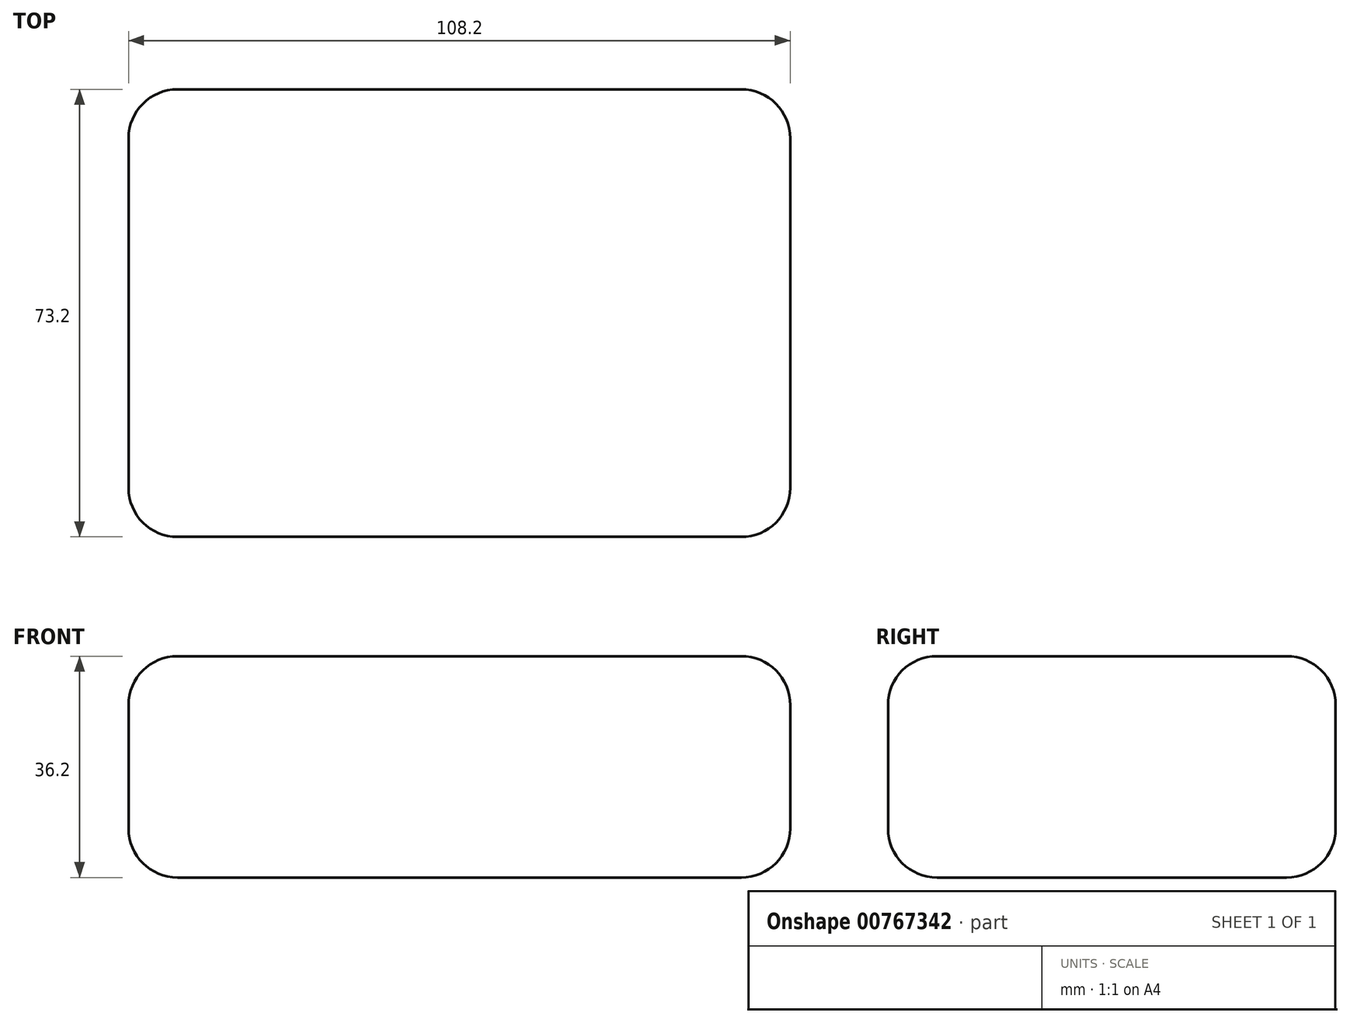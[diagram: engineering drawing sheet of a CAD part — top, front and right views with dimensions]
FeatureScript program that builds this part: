
annotation { "Feature Type Name" : "Feature", "Feature Type Description" : "" }
export const myFeature = defineFeature(function(context is Context, id is Id, definition is map)
    precondition{}
    {
        {
            var Q0;
            Q0=qCreatedBy(makeId("Top.planeOp"),FACE);
            var sketch = newSketch(context, id + "F0", { "sketchPlane" : qUnion([Q0])});
            skLineSegment(sketch, "E0.bottom", {"start": v(54.1, -36.6) * mm, "end": v(-54.1, -36.6) * mm});
            skLineSegment(sketch, "E0.top", {"start": v(54.1, 36.6) * mm, "end": v(-54.1, 36.6) * mm});
            skLineSegment(sketch, "E0.left", {"start": v(54.1, -36.6) * mm, "end": v(54.1, 36.6) * mm});
            skLineSegment(sketch, "E0.right", {"start": v(-54.1, -36.6) * mm, "end": v(-54.1, 36.6) * mm});
            skPoint(sketch, "E0.middle", {"position": v(0, 0) * mm});
            skSolve(sketch);
        }
        {
            var Q0;
            Q0 = qSketchRegion(id + "F0", true);
            extrude(context, id + "F1", {"entities" : qUnion([Q0]), "depth" : 36.2 * mm, "offsetDistance" : 25 * mm});
        }
        {
            var Q0;
            Q0=makeQuery(id+"F1.opExtrude","CAP_FACE",FACE,{"disambiguationData":[OSD([sQuery(id+"F0.wireOp",EDGE,"E0.bottom"),sQuery(id+"F0.wireOp",EDGE,"E0.top"),sQuery(id+"F0.wireOp",EDGE,"E0.left"),sQuery(id+"F0.wireOp",EDGE,"E0.right")])],"isStart":false});
            var Q1;
            Q1=makeQuery(id+"F1.opExtrude","CAP_EDGE",EDGE,{"disambiguationData":[OSD([sQuery(id+"F0.wireOp",EDGE,"E0.bottom")])],"isStart":true});
            var Q2;
            Q2=makeQuery(id+"F1.opExtrude","CAP_EDGE",EDGE,{"disambiguationData":[OSD([sQuery(id+"F0.wireOp",EDGE,"E0.left")])],"isStart":true});
            var Q3;
            Q3=makeQuery(id+"F1.opExtrude","CAP_FACE",FACE,{"disambiguationData":[OSD([sQuery(id+"F0.wireOp",EDGE,"E0.bottom"),sQuery(id+"F0.wireOp",EDGE,"E0.top"),sQuery(id+"F0.wireOp",EDGE,"E0.left"),sQuery(id+"F0.wireOp",EDGE,"E0.right")])],"isStart":true});
            var Q4;
            Q4=makeQuery(id+"F1.opExtrude","SWEPT_FACE",FACE,{"disambiguationData":[OSD([sQuery(id+"F0.wireOp",EDGE,"E0.left")])]});
            var Q5;
            Q5=makeQuery(id+"F1.opExtrude","SWEPT_FACE",FACE,{"disambiguationData":[OSD([sQuery(id+"F0.wireOp",EDGE,"E0.right")])]});
            fillet(context, id + "F2", {"entities" : qUnion([Q0, Q1, Q2, Q3, Q4, Q5]), "radius" : 8 * mm, "tangentPropagation" : true, "allowEdgeOverflow" : false});
        }
    });
